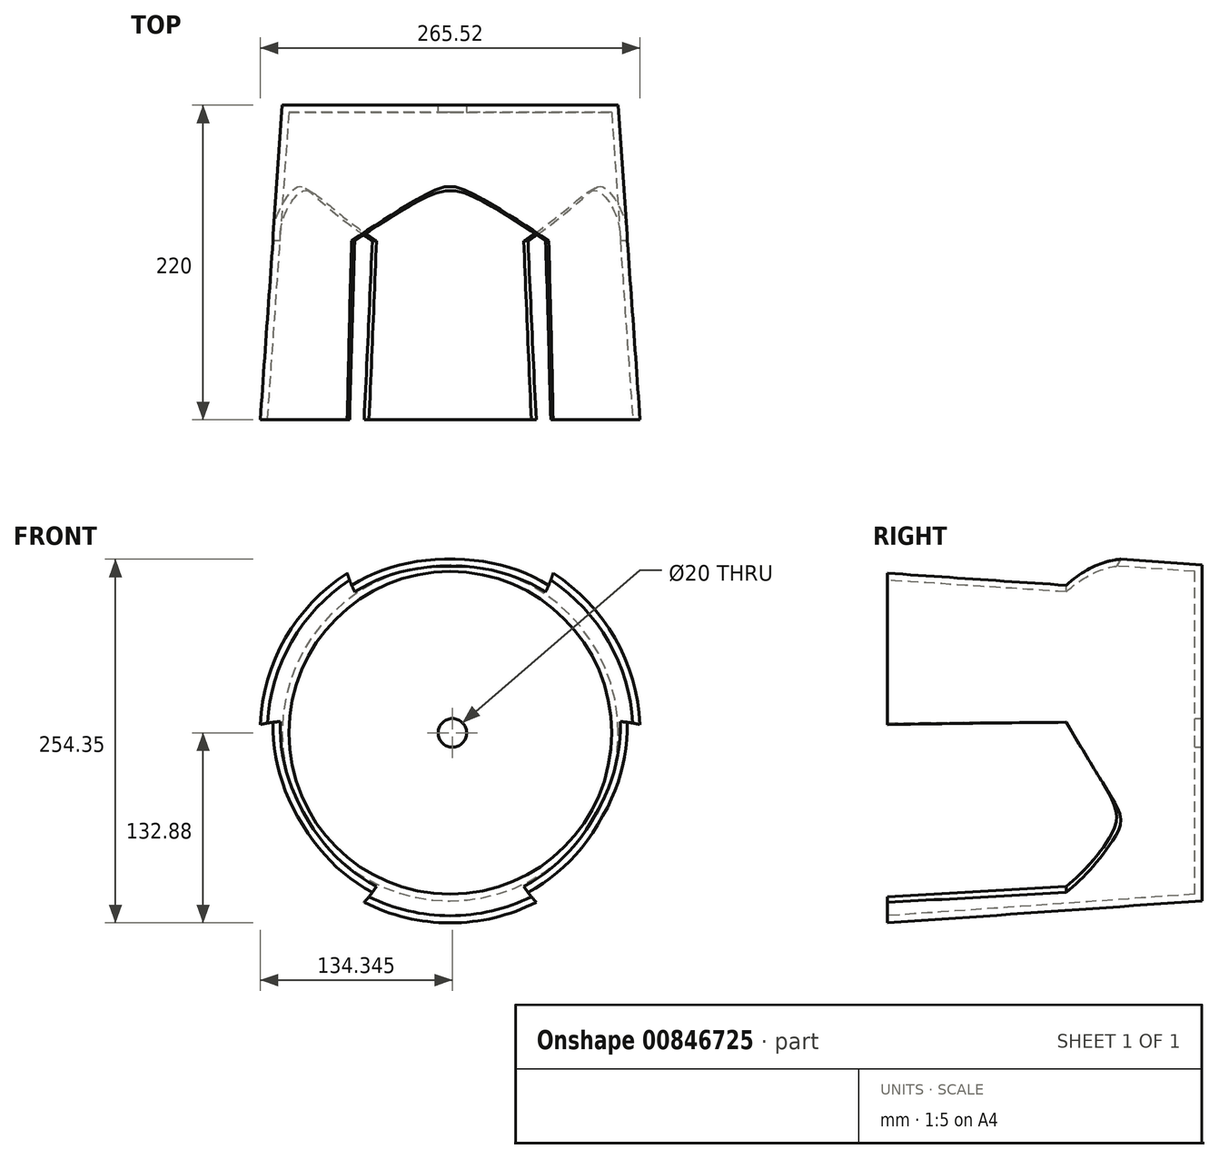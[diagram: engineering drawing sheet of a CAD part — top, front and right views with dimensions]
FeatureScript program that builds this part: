
annotation { "Feature Type Name" : "Feature", "Feature Type Description" : "" }
export const myFeature = defineFeature(function(context is Context, id is Id, definition is map)
    precondition{}
    {
        {
            var Q0;
            Q0=qCreatedBy(makeId("Front.planeOp"),FACE);
            var sketch = newSketch(context, id + "F0", { "sketchPlane" : qUnion([Q0])});
            skCircle(sketch, "E0", {"center": v(0, 0) * mm, "radius": 117.5 * mm});
            skPoint(sketch, "E1", {"position": v(1.58, 0) * mm});
            skSolve(sketch);
        }
        {
            var Q0;
            Q0=makeQuery(id+"F0.imprint","IMPRINT",FACE,{"disambiguationData":[TD([[makeQuery(id+"F0.imprint","IMPRINT",EDGE,{"derivedFrom":sQuery(id+"F0.wireOp",EDGE,"E0")}),1.0]])]});
            extrude(context, id + "F1", {"entities" : qUnion([Q0]), "depth" : 220 * mm, "offsetDistance" : 25.4 * mm, "hasDraft" : true, "draftAngle" : 4 * degree});
        }
        {
            var Q0;
            Q0=makeQuery(id+"F1.opExtrude","CAP_FACE",FACE,{"disambiguationData":[OSD([sQuery(id+"F0.wireOp",EDGE,"E0")])],"isStart":false});
            shell(context, id + "F2", {"entities" : qUnion([Q0]), "thickness" : 5 * mm});
        }
        {
            var Q0;
            Q0=sQuery(id+"F0.wireOp",VERTEX,"E1");
            var Q1;
            Q1=makeQuery(id+"F1.opExtrude","SWEPT_BODY",BODY,{"disambiguationData":[OSD([sQuery(id+"F0.wireOp",EDGE,"E0")])]});
            hole(context, id + "F3", {"style" : HoleStyle.SIMPLE, "endStyle" : HoleEndStyle.BLIND, "oppositeDirection" : true, "holeDiameter" : 20 * mm, "majorDiameter" : 6.35 * mm, "holeDepth" : 200 * mm, "isTappedThrough" : true, "tappedDepth" : 12.7 * mm, "tapClearance" : 3, "locations" : qUnion([Q0]), "scope" : qUnion([Q1])});
        }
        {
            var Q0;
            Q0=makeQuery(id+"F1.opExtrude","CAP_FACE",FACE,{"disambiguationData":[OSD([sQuery(id+"F0.wireOp",EDGE,"E0")])],"isStart":false});
            var sketch = newSketch(context, id + "F4", { "sketchPlane" : qUnion([Q0])});
            skPoint(sketch, "E2", {"position": v(0, 132.88) * mm});
            skPoint(sketch, "E3", {"position": v(-114.75, -67) * mm});
            skPoint(sketch, "E4", {"position": v(114.75, -67) * mm});
            skSolve(sketch);
        }
        {
            var Q0;
            Q0=sQuery(id+"F4.wireOp",VERTEX,"E2");
            var Q1;
            Q1=sQuery(id+"F4.wireOp",VERTEX,"E3");
            var Q2;
            Q2=sQuery(id+"F4.wireOp",VERTEX,"E4");
            var Q3;
            Q3=makeQuery(id+"F1.opExtrude","SWEPT_BODY",BODY,{"disambiguationData":[OSD([sQuery(id+"F0.wireOp",EDGE,"E0")])]});
            hole(context, id + "F5", {"style" : HoleStyle.SIMPLE, "endStyle" : HoleEndStyle.BLIND, "holeDiameter" : 150 * mm, "majorDiameter" : 6.35 * mm, "holeDepth" : 125 * mm, "isTappedThrough" : true, "tappedDepth" : 12.7 * mm, "tapClearance" : 3, "locations" : qUnion([Q0, Q1, Q2]), "scope" : qUnion([Q3])});
        }
    });
